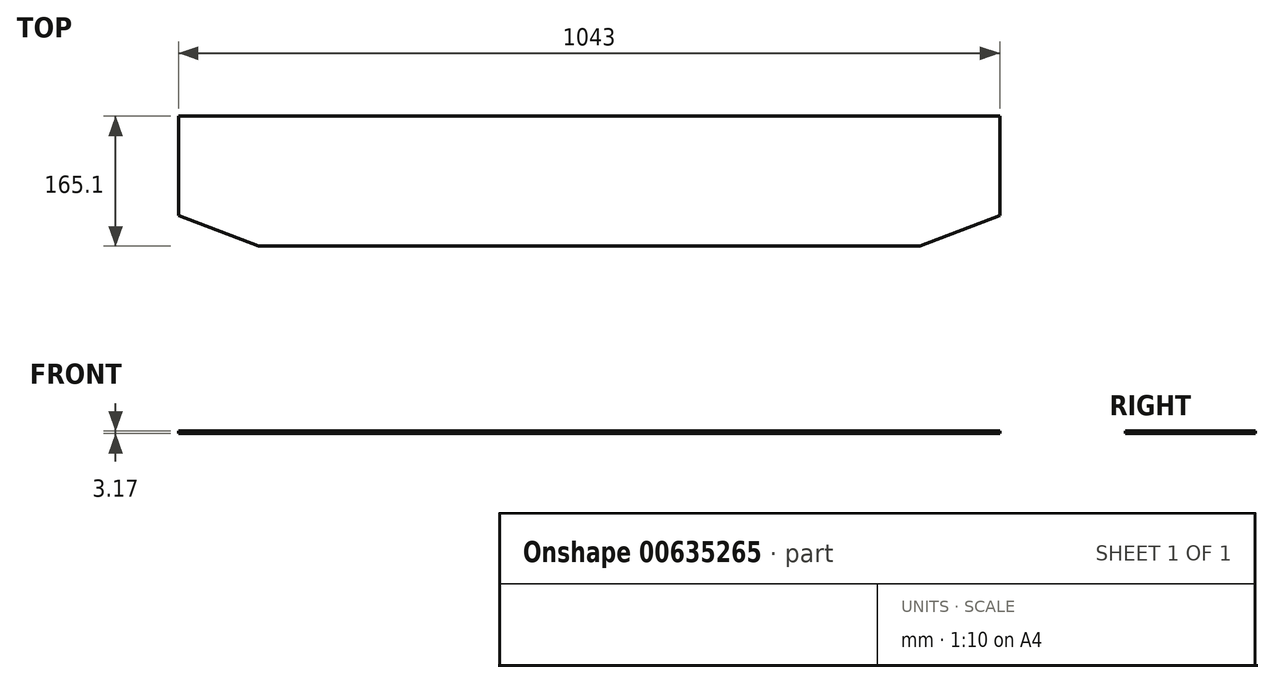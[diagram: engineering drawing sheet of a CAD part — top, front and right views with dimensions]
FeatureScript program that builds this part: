
annotation { "Feature Type Name" : "Feature", "Feature Type Description" : "" }
export const myFeature = defineFeature(function(context is Context, id is Id, definition is map)
    precondition{}
    {
        {
            var Q0;
            Q0=qCreatedBy(makeId("Top.planeOp"),FACE);
            var sketch = newSketch(context, id + "F0", { "sketchPlane" : qUnion([Q0])});
            skLineSegment(sketch, "E0.bottom", {"start": v(521.5, 82.55) * mm, "end": v(-521.5, 82.55) * mm});
            skLineSegment(sketch, "E0.top", {"start": v(419.9, -82.55) * mm, "end": v(-419.9, -82.55) * mm});
            skLineSegment(sketch, "E0.left", {"start": v(521.5, 82.55) * mm, "end": v(521.5, -43.55) * mm});
            skLineSegment(sketch, "E0.right", {"start": v(-521.5, 82.55) * mm, "end": v(-521.5, -43.55) * mm});
            skPoint(sketch, "E0.middle", {"position": v(0, 0) * mm});
            skLineSegment(sketch, "E1", {"start": v(-419.9, -82.55) * mm, "end": v(-521.5, -43.55) * mm});
            skLineSegment(sketch, "E2", {"start": v(419.9, -82.55) * mm, "end": v(521.5, -43.55) * mm});
            skLineSegment(sketch, "E3", {"start": v(-521.5, -82.55) * mm, "end": v(-419.9, -82.55) * mm});
            skLineSegment(sketch, "E4", {"start": v(419.9, -82.55) * mm, "end": v(521.5, -82.55) * mm});
            skSolve(sketch);
        }
        {
            var Q0;
            Q0 = qSketchRegion(id + "F0", true);
            extrude(context, id + "F1", {"entities" : qUnion([Q0]), "depth" : 3.17 * mm, "offsetDistance" : 25.4 * mm});
        }
    });
